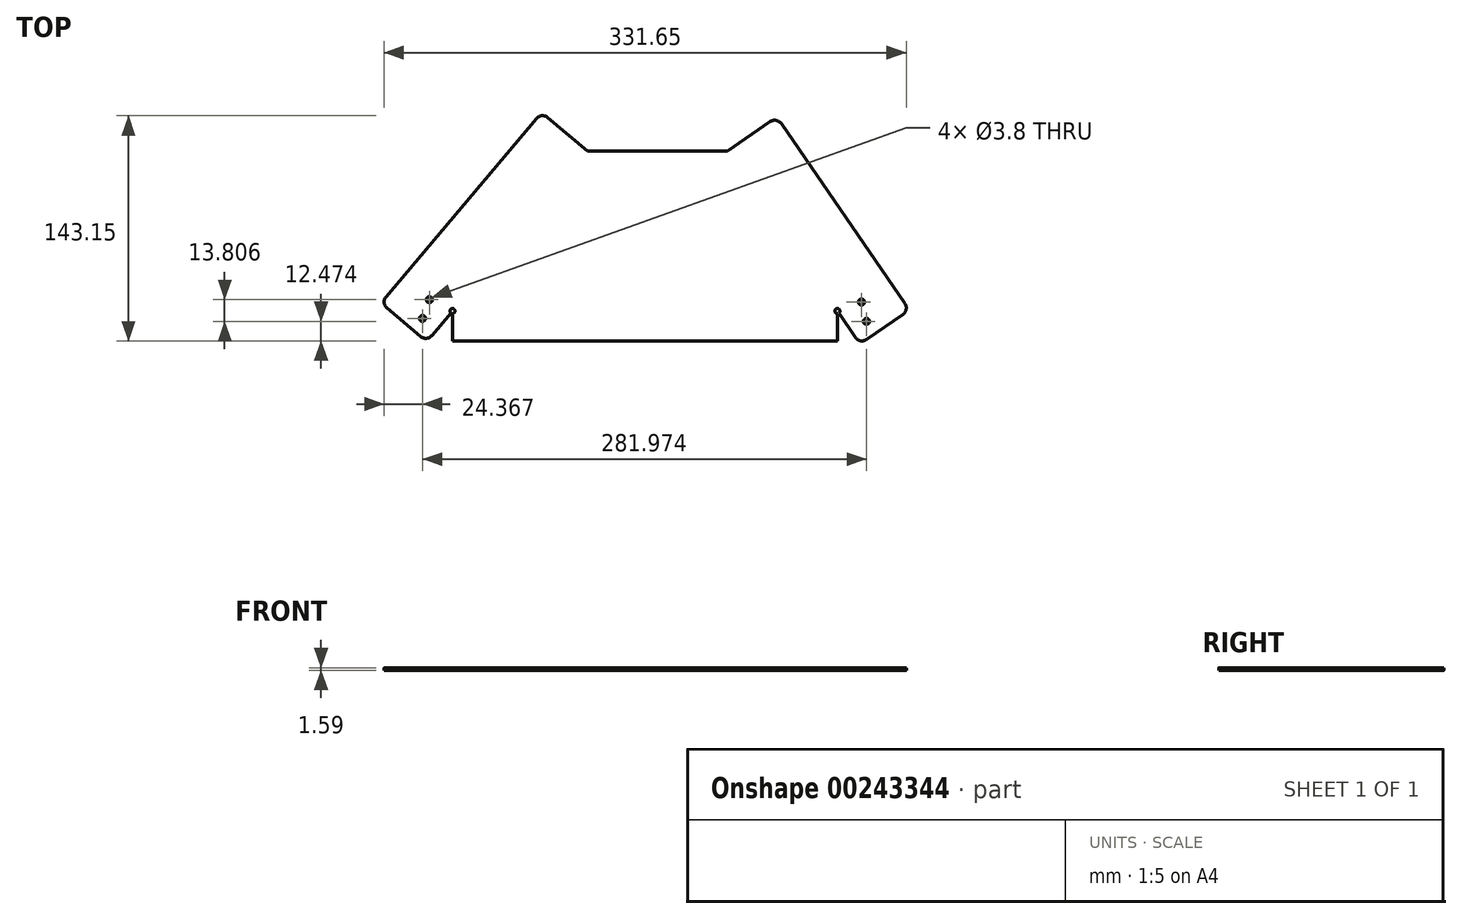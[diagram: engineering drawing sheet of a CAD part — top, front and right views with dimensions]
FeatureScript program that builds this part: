
annotation { "Feature Type Name" : "Feature", "Feature Type Description" : "" }
export const myFeature = defineFeature(function(context is Context, id is Id, definition is map)
    precondition{}
    {
        {
            var Q0;
            Q0=qCreatedBy(makeId("Top.planeOp"),FACE);
            var sketch = newSketch(context, id + "F0", { "sketchPlane" : qUnion([Q0])});
            skLineSegment(sketch, "E0", {"start": v(0, -44.86) * mm, "end": v(-119.06, -44.86) * mm, "construction": true});
            skLineSegment(sketch, "E1", {"start": v(-119.06, -44.86) * mm, "end": v(-33.34, 56.74) * mm});
            skLineSegment(sketch, "E2", {"start": v(-33.34, 56.74) * mm, "end": v(-33.34, 56.74) * mm});
            skLineSegment(sketch, "E3", {"start": v(-33.34, 56.74) * mm, "end": v(0, 56.74) * mm});
            skLineSegment(sketch, "E4.MirrorCS", {"start": v(55.56, 56.74) * mm, "end": v(55.56, 56.74) * mm});
            skLineSegment(sketch, "E5.MirrorCS", {"start": v(125.41, -44.86) * mm, "end": v(55.56, 56.74) * mm});
            skLineSegment(sketch, "E6.MirrorCS", {"start": v(0, -44.86) * mm, "end": v(125.41, -44.86) * mm, "construction": true});
            skLineSegment(sketch, "E7", {"start": v(55.56, 56.74) * mm, "end": v(0, 56.74) * mm});
            skLineSegment(sketch, "E8", {"start": v(-33.34, 56.74) * mm, "end": v(55.56, 56.74) * mm, "construction": true});
            skLineSegment(sketch, "E9.bottom", {"start": v(17.46, 56.74) * mm, "end": v(46.04, 56.74) * mm});
            skLineSegment(sketch, "E10.top", {"start": v(-119.06, -63.9) * mm, "end": v(125.41, -63.9) * mm});
            skLineSegment(sketch, "E10.left", {"start": v(-119.06, -44.86) * mm, "end": v(-119.06, -63.9) * mm});
            skLineSegment(sketch, "E10.right", {"start": v(125.41, -44.86) * mm, "end": v(125.41, -63.9) * mm});
            skLineSegment(sketch, "E11", {"start": v(-33.34, 56.74) * mm, "end": v(-62.46, 81.31) * mm});
            skLineSegment(sketch, "E12", {"start": v(-62.46, 81.31) * mm, "end": v(-164.56, -39.7) * mm});
            skLineSegment(sketch, "E13", {"start": v(-164.56, -39.7) * mm, "end": v(-135.44, -64.27) * mm});
            skLineSegment(sketch, "E14", {"start": v(-135.44, -64.27) * mm, "end": v(-119.06, -44.86) * mm});
            skLineSegment(sketch, "E15", {"start": v(55.56, 56.74) * mm, "end": v(86.91, 78.3) * mm});
            skLineSegment(sketch, "E16", {"start": v(86.91, 78.3) * mm, "end": v(171.15, -44.23) * mm});
            skLineSegment(sketch, "E17", {"start": v(171.15, -44.23) * mm, "end": v(139.76, -65.82) * mm});
            skLineSegment(sketch, "E18", {"start": v(139.76, -65.82) * mm, "end": v(125.41, -44.86) * mm});
            skLineSegment(sketch, "E19", {"start": v(-119.06, -44.86) * mm, "end": v(-148.18, -20.29) * mm, "construction": true});
            skCircle(sketch, "E20", {"center": v(-138.11, -49.55) * mm, "radius": 1.9 * mm});
            skCircle(sketch, "E21", {"center": v(-133.74, -37.63) * mm, "radius": 1.9 * mm});
            skLineSegment(sketch, "E22", {"start": v(-138.11, -49.55) * mm, "end": v(-133.74, -37.63) * mm, "construction": true});
            skLineSegment(sketch, "E23", {"start": v(125.41, -44.86) * mm, "end": v(156.76, -23.3) * mm, "construction": true});
            skCircle(sketch, "E24", {"center": v(140.68, -39.14) * mm, "radius": 1.9 * mm});
            skCircle(sketch, "E25", {"center": v(143.86, -51.44) * mm, "radius": 1.9 * mm});
            skLineSegment(sketch, "E26", {"start": v(140.68, -39.14) * mm, "end": v(143.86, -51.44) * mm, "construction": true});
            skSolve(sketch);
        }
        {
            var Q0;
            Q0=makeQuery(id+"F0.imprint","IMPRINT",FACE,{"disambiguationData":[TD([[makeQuery(id+"F0.imprint","IMPRINT",EDGE,{"derivedFrom":sQuery(id+"F0.wireOp",EDGE,"E1")}),-1.0]])]});
            var Q1;
            Q1=makeQuery(id+"F0.imprint","IMPRINT",FACE,{"disambiguationData":[TD([[makeQuery(id+"F0.imprint","IMPRINT",EDGE,{"derivedFrom":sQuery(id+"F0.wireOp",EDGE,"E1")}),1.0]])]});
            var Q2;
            Q2=makeQuery(id+"F0.imprint","IMPRINT",FACE,{"disambiguationData":[TD([[makeQuery(id+"F0.imprint","IMPRINT",EDGE,{"derivedFrom":sQuery(id+"F0.wireOp",EDGE,"E5.MirrorCS")}),-1.0]])]});
            extrude(context, id + "F1", {"entities" : qUnion([Q0, Q1, Q2]), "depth" : 1.59 * mm});
        }
        {
            var Q0;
            Q0=makeQuery(id+"F1.opExtrude","SWEPT_EDGE",EDGE,{"disambiguationData":[OSD([sQuery(id+"F0.wireOp",EDGE,"E12"),sQuery(id+"F0.wireOp",EDGE,"E13")])]});
            var Q1;
            Q1=makeQuery(id+"F1.opExtrude","SWEPT_EDGE",EDGE,{"disambiguationData":[OSD([sQuery(id+"F0.wireOp",EDGE,"E13"),sQuery(id+"F0.wireOp",EDGE,"E14")])]});
            var Q2;
            Q2=makeQuery(id+"F1.opExtrude","SWEPT_EDGE",EDGE,{"disambiguationData":[OSD([sQuery(id+"F0.wireOp",EDGE,"E17"),sQuery(id+"F0.wireOp",EDGE,"E18")])]});
            var Q3;
            Q3=makeQuery(id+"F1.opExtrude","SWEPT_EDGE",EDGE,{"disambiguationData":[OSD([sQuery(id+"F0.wireOp",EDGE,"E16"),sQuery(id+"F0.wireOp",EDGE,"E17")])]});
            var Q4;
            Q4=makeQuery(id+"F1.opExtrude","SWEPT_EDGE",EDGE,{"disambiguationData":[OSD([sQuery(id+"F0.wireOp",EDGE,"E15"),sQuery(id+"F0.wireOp",EDGE,"E16")])]});
            var Q5;
            Q5=makeQuery(id+"F1.opExtrude","SWEPT_EDGE",EDGE,{"disambiguationData":[OSD([sQuery(id+"F0.wireOp",EDGE,"E11"),sQuery(id+"F0.wireOp",EDGE,"E12")])]});
            fillet(context, id + "F2", {"entities" : qUnion([Q0, Q1, Q2, Q3, Q4, Q5]), "radius" : 5.08 * mm, "tangentPropagation" : true, "allowEdgeOverflow" : false});
        }
        {
            var Q0;
            Q0=makeQuery(id+"F1.opExtrude","CAP_FACE",FACE,{"disambiguationData":[OSD([sQuery(id+"F0.wireOp",EDGE,"E3"),sQuery(id+"F0.wireOp",EDGE,"E7"),sQuery(id+"F0.wireOp",EDGE,"E9.bottom"),sQuery(id+"F0.wireOp",EDGE,"E10.top"),sQuery(id+"F0.wireOp",EDGE,"E10.left"),sQuery(id+"F0.wireOp",EDGE,"E10.right"),sQuery(id+"F0.wireOp",EDGE,"E11"),sQuery(id+"F0.wireOp",EDGE,"E12"),sQuery(id+"F0.wireOp",EDGE,"E13"),sQuery(id+"F0.wireOp",EDGE,"E14"),sQuery(id+"F0.wireOp",EDGE,"E15"),sQuery(id+"F0.wireOp",EDGE,"E16"),sQuery(id+"F0.wireOp",EDGE,"E17"),sQuery(id+"F0.wireOp",EDGE,"E18"),sQuery(id+"F0.wireOp",EDGE,"E20"),sQuery(id+"F0.wireOp",EDGE,"E21"),sQuery(id+"F0.wireOp",EDGE,"E24"),sQuery(id+"F0.wireOp",EDGE,"E25")])],"isStart":false});
            var sketch = newSketch(context, id + "F3", { "sketchPlane" : qUnion([Q0])});
            skCircle(sketch, "E27", {"center": v(-119.06, -44.86) * mm, "radius": 1.59 * mm});
            skCircle(sketch, "E28", {"center": v(125.41, -44.86) * mm, "radius": 1.59 * mm});
            skSolve(sketch);
        }
        {
            var Q0;
            {var subQ0=sQuery(id+"F3.wireOp",EDGE,"E28");var subQ1=makeQuery(id+"F1.opExtrude","CAP_EDGE",EDGE,{"disambiguationData":[OSD([sQuery(id+"F0.wireOp",EDGE,"E10.right")])],"isStart":false});var subQ2=makeQuery(id+"F3.imprint","INTERSECT",VERTEX,{"derivedFrom":[subQ1,subQ0]});Q0=makeQuery(id+"F3.imprint","IMPRINT",FACE,{"disambiguationData":[TD([[makeQuery(id+"F3.imprint","IMPRINT",EDGE,{"disambiguationData":[TD([[subQ2,1.0]])],"derivedFrom":subQ0}),1.0]])]});}
            var Q1;
            {var subQ0=sQuery(id+"F3.wireOp",EDGE,"E27");var subQ1=makeQuery(id+"F1.opExtrude","CAP_EDGE",EDGE,{"disambiguationData":[OSD([sQuery(id+"F0.wireOp",EDGE,"E10.left")])],"isStart":false});var subQ2=makeQuery(id+"F3.imprint","INTERSECT",VERTEX,{"derivedFrom":[subQ1,subQ0]});Q1=makeQuery(id+"F3.imprint","IMPRINT",FACE,{"disambiguationData":[TD([[makeQuery(id+"F3.imprint","IMPRINT",EDGE,{"disambiguationData":[TD([[subQ2,-1.0]])],"derivedFrom":subQ0}),1.0]])]});}
            var Q2;
            Q2=makeQuery(id+"F1.opExtrude","CAP_FACE",FACE,{"disambiguationData":[OSD([sQuery(id+"F0.wireOp",EDGE,"E3"),sQuery(id+"F0.wireOp",EDGE,"E7"),sQuery(id+"F0.wireOp",EDGE,"E9.bottom"),sQuery(id+"F0.wireOp",EDGE,"E10.top"),sQuery(id+"F0.wireOp",EDGE,"E10.left"),sQuery(id+"F0.wireOp",EDGE,"E10.right"),sQuery(id+"F0.wireOp",EDGE,"E11"),sQuery(id+"F0.wireOp",EDGE,"E12"),sQuery(id+"F0.wireOp",EDGE,"E13"),sQuery(id+"F0.wireOp",EDGE,"E14"),sQuery(id+"F0.wireOp",EDGE,"E15"),sQuery(id+"F0.wireOp",EDGE,"E16"),sQuery(id+"F0.wireOp",EDGE,"E17"),sQuery(id+"F0.wireOp",EDGE,"E18"),sQuery(id+"F0.wireOp",EDGE,"E20"),sQuery(id+"F0.wireOp",EDGE,"E21"),sQuery(id+"F0.wireOp",EDGE,"E24"),sQuery(id+"F0.wireOp",EDGE,"E25")])],"isStart":true});
            extrude(context, id + "F4", {"entities" : qUnion([Q0, Q1]), "operationType" : NewBodyOperationType.REMOVE, "endBound" : BoundingType.UP_TO_SURFACE, "oppositeDirection" : true, "endBoundEntityFace" : qUnion([Q2]), "depth" : 25.4 * mm});
        }
    });
